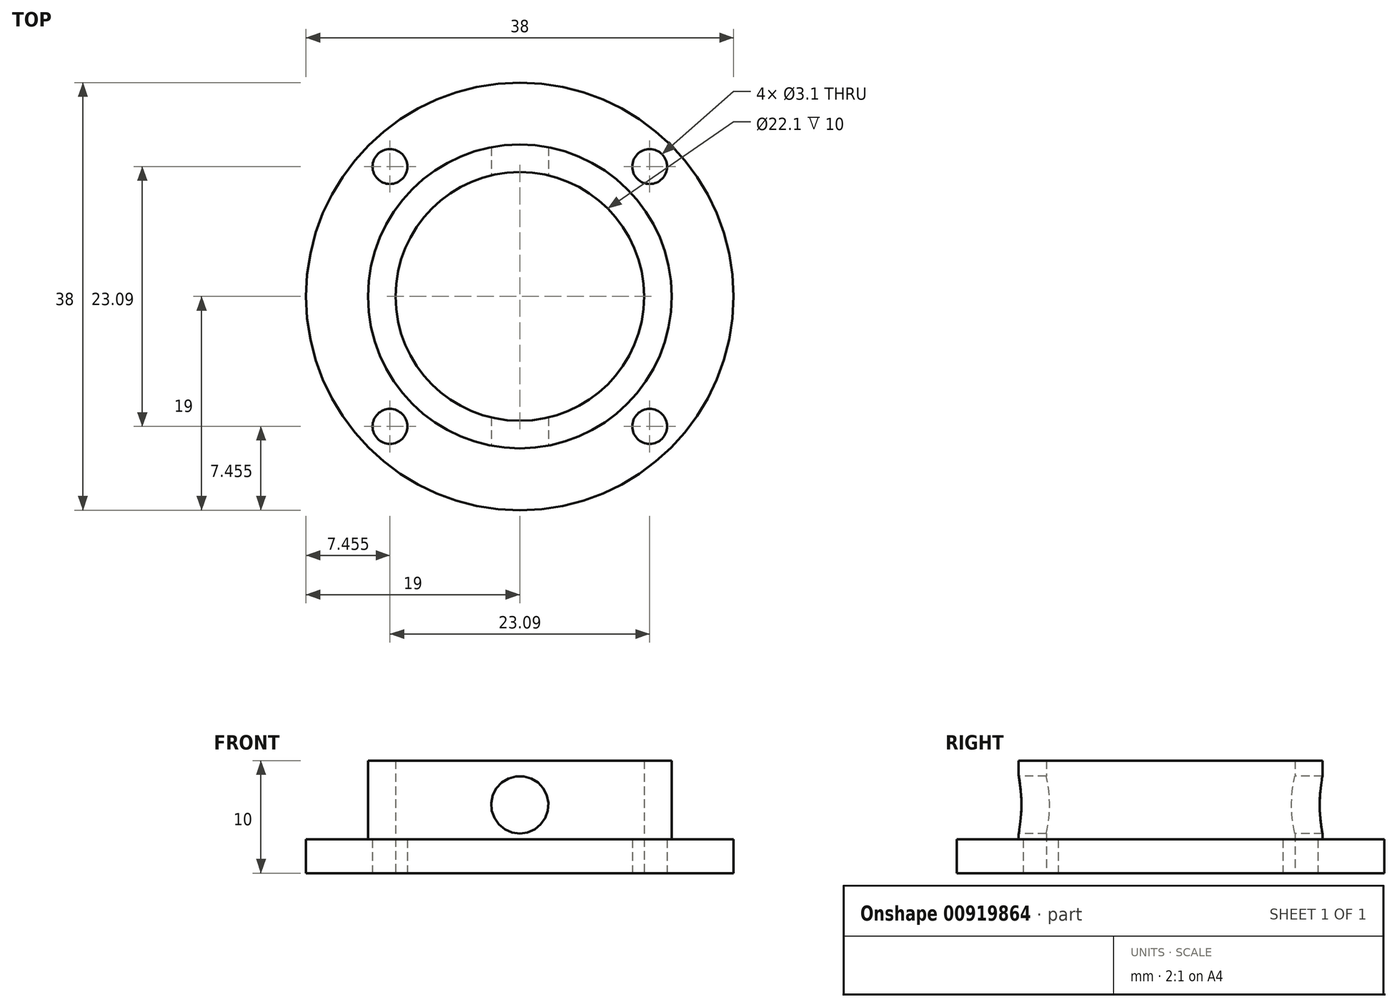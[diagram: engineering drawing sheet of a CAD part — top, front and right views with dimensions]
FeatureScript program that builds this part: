
annotation { "Feature Type Name" : "Feature", "Feature Type Description" : "" }
export const myFeature = defineFeature(function(context is Context, id is Id, definition is map)
    precondition{}
    {
        {
            var Q0;
            Q0=qCreatedBy(makeId("Top.planeOp"),FACE);
            var sketch = newSketch(context, id + "F0", { "sketchPlane" : qUnion([Q0])});
            skCircle(sketch, "E0", {"center": v(0, 0) * mm, "radius": 13.5 * mm});
            skCircle(sketch, "E1", {"center": v(0, 0) * mm, "radius": 11.05 * mm});
            skLineSegment(sketch, "E2", {"start": v(0, 0) * mm, "end": v(0, -13.5) * mm, "construction": true});
            skPoint(sketch, "E3", {"position": v(0, -17.66) * mm});
            skArc(sketch, "E4", {"start": v(-4.63, -12.68) * mm, "mid": v(0, -13.5) * mm, "end": v(4.63, -12.68) * mm});
            skSolve(sketch);
        }
        {
            var Q0;
            Q0=makeQuery(id+"F0.imprint","IMPRINT",FACE,{"disambiguationData":[TD([[makeQuery(id+"F0.imprint","IMPRINT",EDGE,{"derivedFrom":sQuery(id+"F0.wireOp",EDGE,"E0")}),1.0]])]});
            extrude(context, id + "F1", {"entities" : qUnion([Q0]), "depth" : 10 * mm, "offsetDistance" : 25 * mm});
        }
        {
            var Q0;
            Q0=qCreatedBy(makeId("Front.planeOp"),FACE);
            cPlane(context, id + "F2", {"entities" : qUnion([Q0]), "cplaneType" : CPlaneType.OFFSET, "offset" : 9.75 * mm, "width" : 150 * mm, "height" : 150 * mm});
        }
        {
            var Q0;
            Q0=qCreatedBy(id+"F2.planeOp",FACE);
            var sketch = newSketch(context, id + "F3", { "sketchPlane" : qUnion([Q0])});
            skLineSegment(sketch, "E5", {"start": v(0, 0) * mm, "end": v(0, 5) * mm, "construction": true});
            skPoint(sketch, "E6", {"position": v(0, 5) * mm});
            skCircle(sketch, "E7", {"center": v(0, 5) * mm, "radius": 2.5 * mm});
            skSolve(sketch);
        }
        {
            var Q0;
            Q0=sQuery(id+"F3.wireOp",VERTEX,"E6");
            var Q1;
            Q1=makeQuery(id+"F1.opExtrude","SWEPT_BODY",BODY,{"disambiguationData":[OSD([sQuery(id+"F0.wireOp",EDGE,"E0"),sQuery(id+"F0.wireOp",EDGE,"E1")])]});
            hole(context, id + "F4", {"style" : HoleStyle.SIMPLE, "endStyle" : HoleEndStyle.BLIND, "holeDiameter" : 5 * mm, "majorDiameter" : 5 * mm, "holeDepth" : 19.5 * mm, "isTappedThrough" : true, "tappedDepth" : 12 * mm, "tapClearance" : 3, "startFromSketch" : true, "locations" : qUnion([Q0]), "scope" : qUnion([Q1])});
        }
        {
            var Q0;
            Q0=qCreatedBy(makeId("Top.planeOp"),FACE);
            var sketch = newSketch(context, id + "F5", { "sketchPlane" : qUnion([Q0])});
            skCircle(sketch, "E8", {"center": v(0, 0) * mm, "radius": 13.5 * mm});
            skCircle(sketch, "E9", {"center": v(0, 0) * mm, "radius": 19 * mm});
            skPoint(sketch, "E10", {"position": v(0, 16.33) * mm});
            skCircle(sketch, "E11.1.0", {"center": v(-11.54, 11.54) * mm, "radius": 1.55 * mm});
            skCircle(sketch, "E11.3.0", {"center": v(-11.54, -11.54) * mm, "radius": 1.55 * mm});
            skCircle(sketch, "E12.1.5.0", {"center": v(11.54, -11.54) * mm, "radius": 1.55 * mm});
            skCircle(sketch, "E12.1.7.0", {"center": v(11.54, 11.54) * mm, "radius": 1.55 * mm});
            skSolve(sketch);
        }
        {
            var Q0;
            Q0=makeQuery(id+"F5.imprint","IMPRINT",FACE,{"disambiguationData":[TD([[makeQuery(id+"F5.imprint","IMPRINT",EDGE,{"derivedFrom":sQuery(id+"F5.wireOp",EDGE,"E8")}),-1.0]])]});
            extrude(context, id + "F6", {"entities" : qUnion([Q0]), "operationType" : NewBodyOperationType.ADD, "depth" : 3 * mm, "offsetDistance" : 25 * mm});
        }
        {
            var Q0;
            Q0=qCreatedBy(id+"F2.planeOp",FACE);
            cPlane(context, id + "F7", {"entities" : qUnion([Q0]), "cplaneType" : CPlaneType.OFFSET, "offset" : 3.9 * mm, "width" : 150 * mm, "height" : 150 * mm});
        }
        {
            var Q0;
            Q0=qCreatedBy(id+"F7.planeOp",FACE);
            var sketch = newSketch(context, id + "F8", { "sketchPlane" : qUnion([Q0])});
            skPoint(sketch, "E13", {"position": v(0, 6.08) * mm});
            skSolve(sketch);
        }
        {
            var Q0;
            Q0=sQuery(id+"F8.wireOp",VERTEX,"E13");
            var Q1;
            Q1=makeQuery(id+"F1.opExtrude","SWEPT_BODY",BODY,{"disambiguationData":[OSD([sQuery(id+"F0.wireOp",EDGE,"E0"),sQuery(id+"F0.wireOp",EDGE,"E1")])]});
            hole(context, id + "F9", {"style" : HoleStyle.SIMPLE, "endStyle" : HoleEndStyle.THROUGH, "holeDiameter" : 5.1 * mm, "majorDiameter" : 5 * mm, "isTappedThrough" : true, "tappedDepth" : 12 * mm, "tapClearance" : 3, "startFromSketch" : true, "locations" : qUnion([Q0]), "scope" : qUnion([Q1])});
        }
    });
